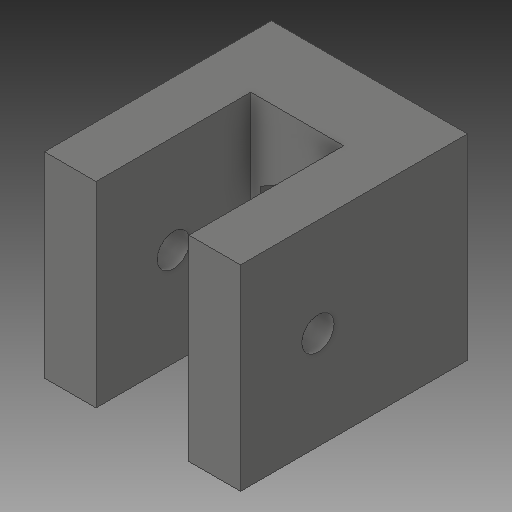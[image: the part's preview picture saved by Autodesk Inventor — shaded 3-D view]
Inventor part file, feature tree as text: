
AUTODESK INVENTOR PART (.ipt)
format: ipt  version: 2019 (Build 230136000, 136)  size: 291,328 bytes
history: native  units: in
note: dims shown in document units (in); Inventor stores cm internally (conversion verified against a paired STEP export)
features: extrude x5, sketch x5, projected_geometry x1
ambient origin geometry x8: Origin, YZ Plane, XZ Plane, XY Plane, X Axis, Y Axis, Z Axis, Center Point
bodies: Solid1 (feature_tree)
feature tree (11):
  extrude  "Extrusion1"  Depth=0.748in
  extrude  "Extrusion2"  Depth=0.3543in
  extrude  "Extrusion3"  Depth=0.5906in
  extrude  "Extrusion4"  Depth=0.5906in
  extrude  "Extrusion5"  Depth=0.126in
  sketch  "Sketch1"  dims[d0=0.748in d1=0.748in]
  sketch  "Sketch2"  dims[d2=0.2756in d3=0.0in d4=0.3543in]
  projected_geometry  "Projected Loop1"
  sketch  "Sketch3"  dims[d5=0.5906in d6=0.0in d7=0.1673in]
  sketch  "Sketch4"  dims[d8=0.5906in d9=0.0in d10=0.124in]
  sketch  "Sketch5"  dims[d11=0.5906in d12=0.0in d13=0.3248in d14=0.126in d15=0.0in]
